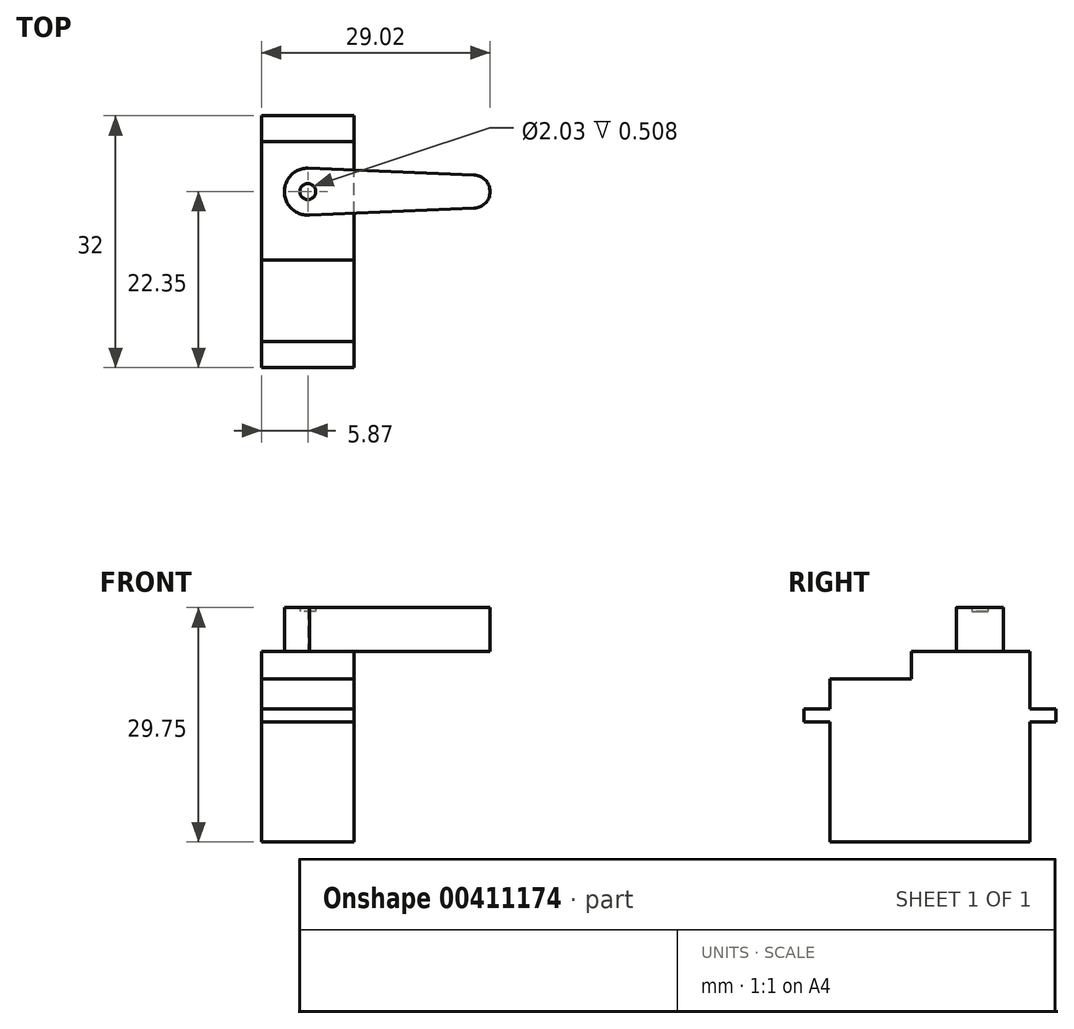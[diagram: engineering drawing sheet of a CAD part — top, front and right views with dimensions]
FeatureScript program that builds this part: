
annotation { "Feature Type Name" : "Feature", "Feature Type Description" : "" }
export const myFeature = defineFeature(function(context is Context, id is Id, definition is map)
    precondition{}
    {
        {
            var Q0;
            Q0=qCreatedBy(makeId("Right.planeOp"),FACE);
            var sketch = newSketch(context, id + "F0", { "sketchPlane" : qUnion([Q0])});
            skLineSegment(sketch, "E0.bottom", {"start": v(12.7, 10.34) * mm, "end": v(-12.7, 10.34) * mm});
            skLineSegment(sketch, "E0.top", {"start": v(12.7, -10.34) * mm, "end": v(-12.7, -10.34) * mm});
            skLineSegment(sketch, "E0.left", {"start": v(12.7, 10.34) * mm, "end": v(12.7, -10.34) * mm});
            skLineSegment(sketch, "E0.right", {"start": v(-12.7, 10.34) * mm, "end": v(-12.7, -10.34) * mm});
            skPoint(sketch, "E0.middle", {"position": v(0, 0) * mm});
            skLineSegment(sketch, "E1", {"start": v(-12.7, 4.88) * mm, "end": v(-16, 4.88) * mm});
            skLineSegment(sketch, "E2", {"start": v(-16, 4.88) * mm, "end": v(-16, 6.53) * mm});
            skLineSegment(sketch, "E3", {"start": v(-16, 6.53) * mm, "end": v(-12.7, 6.53) * mm});
            skLineSegment(sketch, "E4", {"start": v(0, 0) * mm, "end": v(0, 30.75) * mm, "construction": true});
            skLineSegment(sketch, "E5.MirrorCS", {"start": v(16, 6.53) * mm, "end": v(12.7, 6.53) * mm});
            skLineSegment(sketch, "E6.MirrorCS", {"start": v(12.7, 4.88) * mm, "end": v(16, 4.88) * mm});
            skLineSegment(sketch, "E7.MirrorCS", {"start": v(16, 4.88) * mm, "end": v(16, 6.53) * mm});
            skLineSegment(sketch, "E8", {"start": v(-2.36, 10.34) * mm, "end": v(-2.36, 13.82) * mm});
            skLineSegment(sketch, "E9", {"start": v(-2.36, 13.82) * mm, "end": v(12.7, 13.82) * mm});
            skLineSegment(sketch, "E10", {"start": v(12.7, 13.82) * mm, "end": v(12.7, 10.34) * mm});
            skSolve(sketch);
        }
        {
            var Q0;
            {var subQ4=sQuery(id+"F0.wireOp",EDGE,"E0.top");Q0=makeQuery(id+"F0.imprint","IMPRINT",FACE,{"disambiguationData":[TD([[makeQuery(id+"F0.imprint","IMPRINT",EDGE,{"derivedFrom":subQ4}),-1.0]])]});}
            var Q1;
            {var subQ0=sQuery(id+"F0.wireOp",EDGE,"E1");Q1=makeQuery(id+"F0.imprint","IMPRINT",FACE,{"disambiguationData":[TD([[makeQuery(id+"F0.imprint","IMPRINT",EDGE,{"derivedFrom":subQ0}),-1.0]])]});}
            var Q2;
            {var subQ2=sQuery(id+"F0.wireOp",EDGE,"E8");Q2=makeQuery(id+"F0.imprint","IMPRINT",FACE,{"disambiguationData":[TD([[makeQuery(id+"F0.imprint","IMPRINT",EDGE,{"derivedFrom":subQ2}),-1.0]])]});}
            var Q3;
            {var subQ0=sQuery(id+"F0.wireOp",EDGE,"E5.MirrorCS");Q3=makeQuery(id+"F0.imprint","IMPRINT",FACE,{"disambiguationData":[TD([[makeQuery(id+"F0.imprint","IMPRINT",EDGE,{"derivedFrom":subQ0}),1.0]])]});}
            extrude(context, id + "F1", {"entities" : qUnion([Q0, Q1, Q2, Q3]), "endBound" : BoundingType.SYMMETRIC, "depth" : 11.75 * mm});
        }
        {
            var Q0;
            Q0=makeQuery(id+"F1.opExtrude","SWEPT_FACE",FACE,{"disambiguationData":[OSD([sQuery(id+"F0.wireOp",EDGE,"E9")])]});
            var sketch = newSketch(context, id + "F2", { "sketchPlane" : qUnion([Q0])});
            skArc(sketch, "E11", {"start": v(0, 9.33) * mm, "mid": v(-2.98, 6.23) * mm, "end": v(0.25, 3.38) * mm});
            skArc(sketch, "E12", {"start": v(21.13, 4.24) * mm, "mid": v(23.15, 6.35) * mm, "end": v(21.13, 8.46) * mm});
            skLineSegment(sketch, "E13", {"start": v(0, 6.35) * mm, "end": v(21.04, 6.35) * mm, "construction": true});
            skLineSegment(sketch, "E14", {"start": v(0, 9.33) * mm, "end": v(21.13, 8.46) * mm});
            skLineSegment(sketch, "E15", {"start": v(0, 3.37) * mm, "end": v(21.13, 4.24) * mm});
            skCircle(sketch, "E16", {"center": v(0, 6.35) * mm, "radius": 1.02 * mm});
            skSolve(sketch);
        }
        {
            var Q0;
            Q0 = qSketchRegion(id + "F2", true);
            extrude(context, id + "F3", {"entities" : qUnion([Q0]), "depth" : 5.6 * mm});
        }
        {
            var Q0;
            Q0=makeQuery(id+"F2.imprint","IMPRINT",FACE,{"disambiguationData":[TD([[makeQuery(id+"F2.imprint","IMPRINT",EDGE,{"derivedFrom":sQuery(id+"F2.wireOp",EDGE,"E16")}),1.0]])]});
            extrude(context, id + "F4", {"entities" : qUnion([Q0]), "operationType" : NewBodyOperationType.ADD, "depth" : 5.08 * mm});
        }
    });
